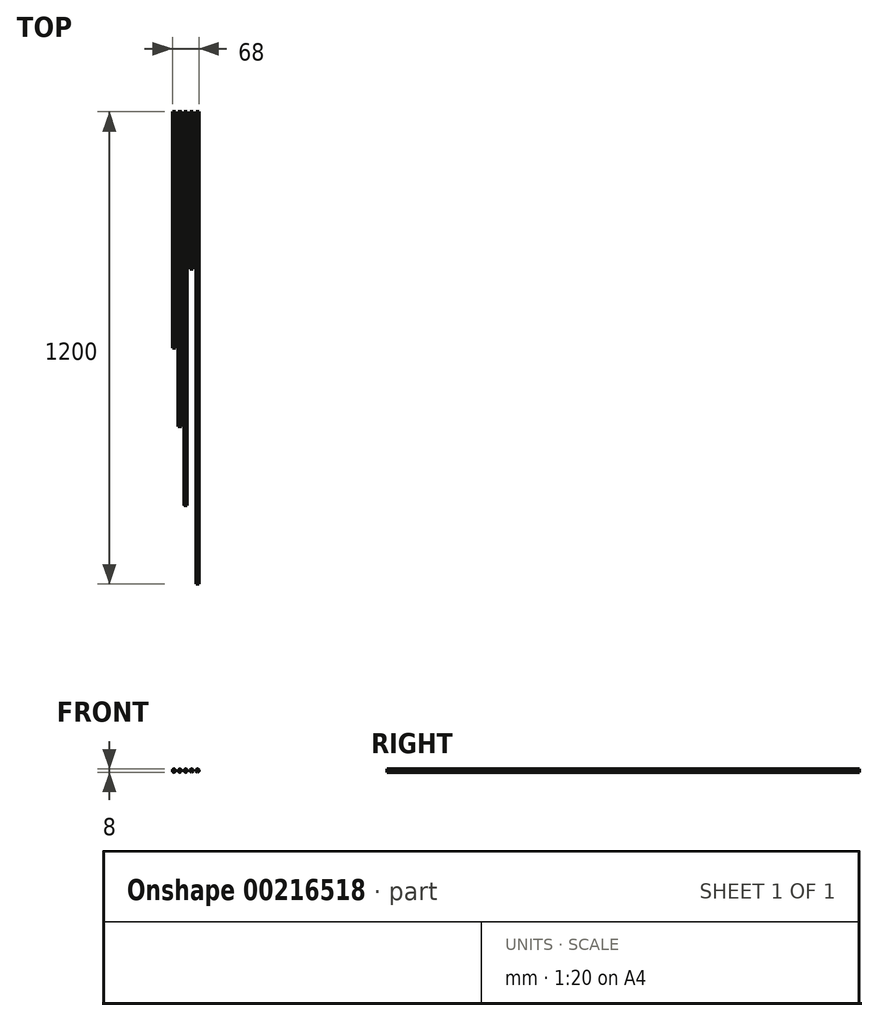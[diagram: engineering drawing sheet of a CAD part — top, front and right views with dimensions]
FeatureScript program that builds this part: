
annotation { "Feature Type Name" : "Feature", "Feature Type Description" : "" }
export const myFeature = defineFeature(function(context is Context, id is Id, definition is map)
    precondition{}
    {
        {
            var Q0;
            Q0=qCreatedBy(makeId("Front.planeOp"),FACE);
            var sketch = newSketch(context, id + "F0", { "sketchPlane" : qUnion([Q0])});
            skCircle(sketch, "E0", {"center": v(0, 0) * mm, "radius": 4 * mm});
            skCircle(sketch, "E1", {"center": v(15, 0) * mm, "radius": 4 * mm});
            skCircle(sketch, "E2", {"center": v(30, 0) * mm, "radius": 4 * mm});
            skCircle(sketch, "E3", {"center": v(-15, 0) * mm, "radius": 4 * mm});
            skCircle(sketch, "E4", {"center": v(-30, 0) * mm, "radius": 4 * mm});
            skSolve(sketch);
        }
        {
            var Q0;
            Q0=makeQuery(id+"F0.imprint","IMPRINT",FACE,{"disambiguationData":[TD([[makeQuery(id+"F0.imprint","IMPRINT",EDGE,{"derivedFrom":sQuery(id+"F0.wireOp",EDGE,"E0")}),1.0]])]});
            extrude(context, id + "F1", {"entities" : qUnion([Q0]), "depth" : 1000 * mm});
        }
        {
            var Q0;
            Q0=makeQuery(id+"F0.imprint","IMPRINT",FACE,{"disambiguationData":[TD([[makeQuery(id+"F0.imprint","IMPRINT",EDGE,{"derivedFrom":sQuery(id+"F0.wireOp",EDGE,"E3")}),1.0]])]});
            var Q1;
            Q1=sQuery(id+"F0.wireOp",EDGE,"E3");
            extrude(context, id + "F2", {"entities" : qUnion([Q0]), "surfaceEntities" : qUnion([Q1]), "depth" : 800 * mm});
        }
        {
            var Q0;
            Q0=makeQuery(id+"F0.imprint","IMPRINT",FACE,{"disambiguationData":[TD([[makeQuery(id+"F0.imprint","IMPRINT",EDGE,{"derivedFrom":sQuery(id+"F0.wireOp",EDGE,"E4")}),1.0]])]});
            extrude(context, id + "F3", {"entities" : qUnion([Q0]), "depth" : 600 * mm});
        }
        {
            var Q0;
            Q0=makeQuery(id+"F0.imprint","IMPRINT",FACE,{"disambiguationData":[TD([[makeQuery(id+"F0.imprint","IMPRINT",EDGE,{"derivedFrom":sQuery(id+"F0.wireOp",EDGE,"E1")}),1.0]])]});
            var Q1;
            Q1=qConstructionFilter(qBodyType(qCreatedBy(id+"F0",EDGE),BodyType.WIRE),ConstructionObject.NO);
            extrude(context, id + "F4", {"entities" : qUnion([Q0]), "surfaceEntities" : qUnion([Q1]), "depth" : 400 * mm});
        }
        {
            var Q0;
            Q0=makeQuery(id+"F0.imprint","IMPRINT",FACE,{"disambiguationData":[TD([[makeQuery(id+"F0.imprint","IMPRINT",EDGE,{"derivedFrom":sQuery(id+"F0.wireOp",EDGE,"E2")}),1.0]])]});
            extrude(context, id + "F5", {"entities" : qUnion([Q0]), "depth" : 1200 * mm});
        }
    });
